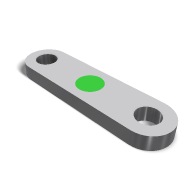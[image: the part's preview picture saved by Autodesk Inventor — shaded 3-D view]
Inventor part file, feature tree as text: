
AUTODESK INVENTOR PART (.ipt)
format: ipt  version: 2016 (Build 200138000, 138)  size: 100,864 bytes
history: native  units: mm
features: fillet x2, hole x2, sketch x2, extrude x1, split x1
ambient origin geometry x8: Origin, YZ Plane, XZ Plane, XY Plane, X Axis, Y Axis, Z Axis, Center Point
bodies: Solid1 (feature_tree)
feature tree (8):
  extrude  "Extrusion1"  Depth=30.0mm
  fillet  "Fillet1"  Radius=10.0mm
  fillet  "Fillet2"  Radius=10.0mm
  hole  "Hole1"  [1 undecoded]
  hole  "Hole2"  [1 undecoded]
  split  "Split1"
  sketch  "Sketch1"  dims[d0=115.0mm d1=30.0mm d2=10.0mm d3=0.0mm]
  sketch  "Sketch2"  dims[d22=10.0mm d23=10.0mm d6=15.0mm d7=6.0mm d8=23.78mm d9=7.95mm d10=90.0deg d11=8.0mm d12=20.594885mm d13=10.0mm d14=10.0mm d15=15.0mm d16=6.0mm d17=23.78mm d18=7.76mm d19=90.0deg d20=8.0mm d21=20.594885mm d24=18.0mm]
note: 2 required parameter values undecoded (feature->parameter linkage not recoverable at this tier; creation-order binding heuristic only, values carry confidence <= 0.55)
